# Revit family: Domotics-DomesticRanges-GEWISS-CHORUS_DATA-CONNECTOR_USB
name_source: partatom
category: Apparecchi elettrici
revit_build: Autodesk Revit 2016 (Build: 20161004_0715(x64)
units: mm (PartAtom-declared; Revit-internal decimal feet)

## family parameters
Condiviso = No
Host = Muro
Mantenere orientamento annotazione = Sì
Punto di calcolo locali = No
Quota connettore circolare = Usa diametro
Sempre verticale = Sì
Taglio con vuoti quando caricato = No
Tipo di parte = Normale

## types (3) — shared parameters
Catalogue = DOMOTICS
Catalogue Range = CHORUS - DOMESTIC RANGE
Category = Socket-outlet
Description. = Socket-outlet
Description: = USB socket-outlet
Dettagli tipo 1 = No
Dettaglio tipi 2 -3 = Sì
Electrocod = 3720
IDF = f0fdc250-31af-41ad-8c7f-b97bad5e82b7
IDT = ce8da596-15d8-4854-9f17-e6a31c73b8ce
Immagine tipo = GW14459.jpg
Larghezza = 27 mm  [stored 0.0885827 ft]
Materiale = GEWISS TITANIO
No. Chorus modules = 1
No. Chorus modules: = 1
Produttore = GEWISS S.p.A.
SEO = Socket outlet
Technical sheet = https://www.gewiss.com
URL = https://www.gewiss.com
Version file RFA = 19.0

## per-type parameters (varying)
| type | Colour | Descrizione | EAN code | Modello |
| GW12459 - USB socket outlet 1M Black | Black | USB SOCKET OUTLET 1M BLACK | 8011564780767 | GW12459 |
| GW14459 - USB socket outlet 1M Titanium | Titanium | USB SOCKET OUTLET 1M TITANIUM | 8011564780774 | GW14459 |
| GW10459 - USB socket outlet 1M White | White | USB SOCKET OUTLET 1M WHITE | 8011564780750 | GW10459 |

note: [stored X ft] marks values corroborated as IEEE doubles in the binary element streams (Revit-internal decimal feet)

## geometry (parser evidence)
native form markers: Sweep x2
no freeform markers — native parametric forms only
